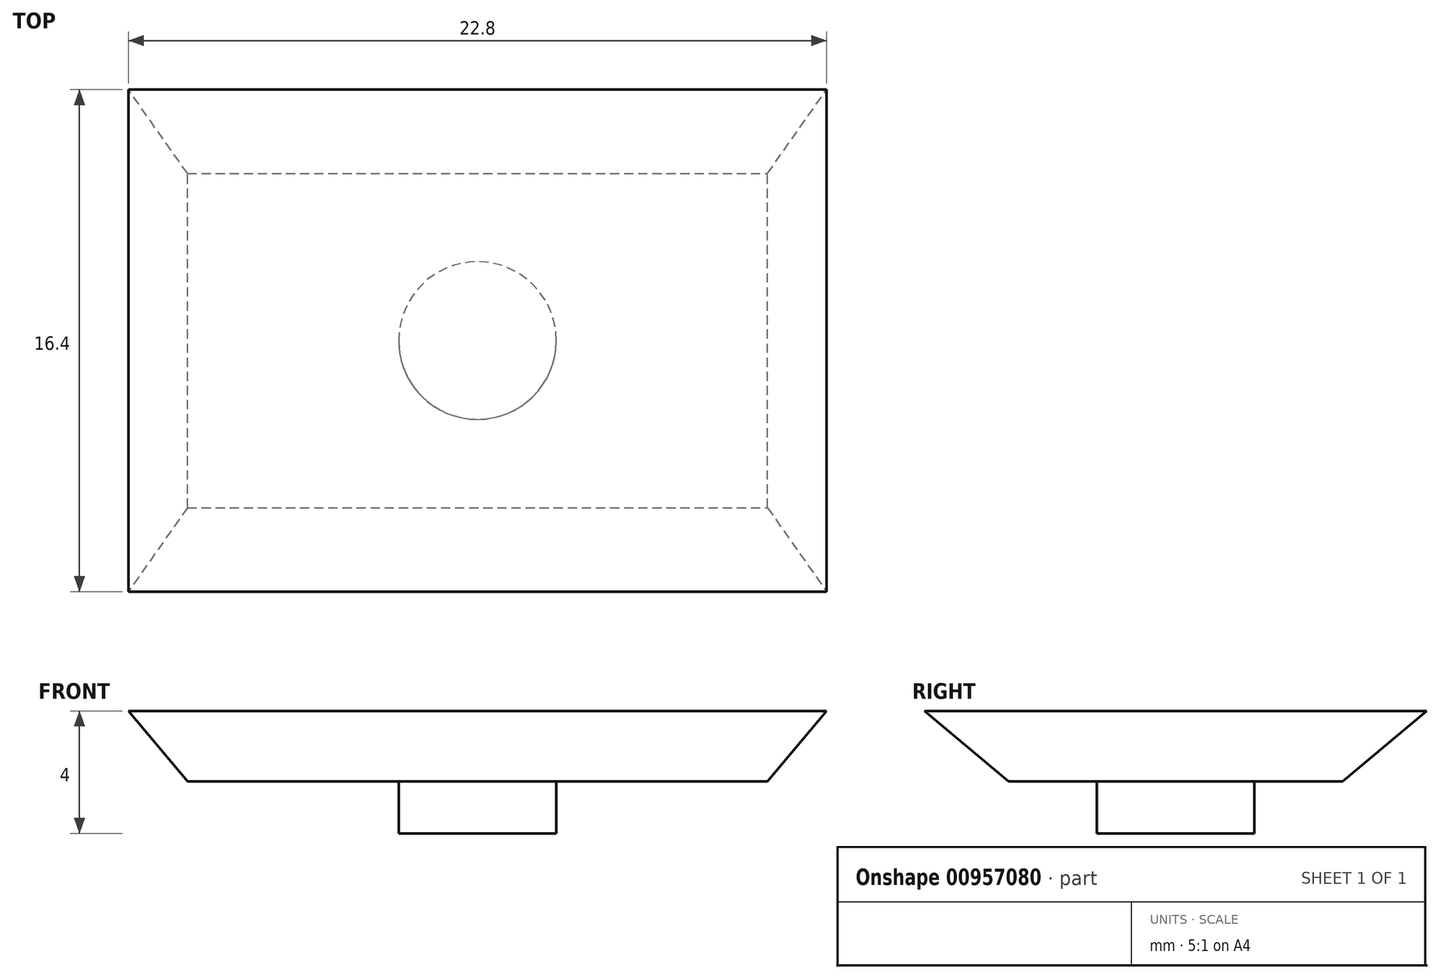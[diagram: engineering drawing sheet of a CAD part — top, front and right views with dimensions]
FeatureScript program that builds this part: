
annotation { "Feature Type Name" : "Feature", "Feature Type Description" : "" }
export const myFeature = defineFeature(function(context is Context, id is Id, definition is map)
    precondition{}
    {
        {
            var Q0;
            Q0=qCreatedBy(makeId("Front.planeOp"),FACE);
            var sketch = newSketch(context, id + "F0", { "sketchPlane" : qUnion([Q0])});
            skLineSegment(sketch, "E0", {"start": v(-15.47, 0) * mm, "end": v(15.77, 0) * mm, "construction": true});
            skLineSegment(sketch, "E1", {"start": v(0, 15.71) * mm, "end": v(0, -11.4) * mm, "construction": true});
            skLineSegment(sketch, "E2", {"start": v(0, 0) * mm, "end": v(9.47, 0) * mm});
            skLineSegment(sketch, "E3", {"start": v(9.47, 0) * mm, "end": v(11.4, 2.3) * mm});
            skLineSegment(sketch, "E4", {"start": v(11.4, 2.3) * mm, "end": v(0, 2.3) * mm});
            skLineSegment(sketch, "E5", {"start": v(9.47, 0) * mm, "end": v(9.47, 3.45) * mm, "construction": true});
            skLineSegment(sketch, "E6.MirrorCS", {"start": v(-11.4, 2.3) * mm, "end": v(0, 2.3) * mm});
            skLineSegment(sketch, "E7.MirrorCS", {"start": v(0, 0) * mm, "end": v(-9.47, 0) * mm});
            skLineSegment(sketch, "E8.MirrorCS", {"start": v(-9.47, 0) * mm, "end": v(-11.4, 2.3) * mm});
            skSolve(sketch);
        }
        {
            var Q0;
            Q0 = qSketchRegion(id + "F0", true);
            extrude(context, id + "F1", {"entities" : qUnion([Q0]), "depth" : 16.4 * mm, "offsetDistance" : 25 * mm});
        }
        {
            var Q0;
            Q0=qCreatedBy(makeId("Right.planeOp"),FACE);
            var sketch = newSketch(context, id + "F2", { "sketchPlane" : qUnion([Q0])});
            skLineSegment(sketch, "E9", {"start": v(0, 0) * mm, "end": v(-2.74, 0) * mm});
            skLineSegment(sketch, "E10", {"start": v(0, 2.3) * mm, "end": v(0, 0) * mm});
            skLineSegment(sketch, "E11", {"start": v(0, 2.3) * mm, "end": v(-2.74, 0) * mm});
            skLineSegment(sketch, "E12", {"start": v(-2.74, 0) * mm, "end": v(-2.74, 2.49) * mm, "construction": true});
            skLineSegment(sketch, "E13", {"start": v(-8.2, 6.19) * mm, "end": v(-8.2, -2.45) * mm, "construction": true});
            skLineSegment(sketch, "E14.MirrorCS", {"start": v(-16.4, 2.3) * mm, "end": v(-13.66, 0) * mm});
            skLineSegment(sketch, "E15.MirrorCS", {"start": v(-16.4, 0) * mm, "end": v(-13.66, 0) * mm});
            skLineSegment(sketch, "E16.MirrorCS", {"start": v(-16.4, 2.3) * mm, "end": v(-16.4, 0) * mm});
            skSolve(sketch);
        }
        {
            var Q0;
            Q0 = qSketchRegion(id + "F2", true);
            extrude(context, id + "F3", {"entities" : qUnion([Q0]), "operationType" : NewBodyOperationType.REMOVE, "endBound" : BoundingType.SYMMETRIC, "oppositeDirection" : true, "depth" : 25 * mm, "offsetDistance" : 25 * mm});
        }
        {
            var Q0;
            Q0=makeQuery(id+"F1.opExtrude","SWEPT_FACE",FACE,{"disambiguationData":[OSD([sQuery(id+"F0.wireOp",EDGE,"E4"),sQuery(id+"F0.wireOp",EDGE,"E6.MirrorCS")])]});
            var sketch = newSketch(context, id + "F4", { "sketchPlane" : qUnion([Q0])});
            skLineSegment(sketch, "E17", {"start": v(-11.4, 0) * mm, "end": v(13.98, 0) * mm, "construction": true});
            skLineSegment(sketch, "E18", {"start": v(0, 0) * mm, "end": v(0, -18.27) * mm, "construction": true});
            skLineSegment(sketch, "E19", {"start": v(-3.63, -8.2) * mm, "end": v(5.01, -8.2) * mm, "construction": true});
            skCircle(sketch, "E20", {"center": v(0, -8.2) * mm, "radius": 2.58 * mm});
            skSolve(sketch);
        }
        {
            var Q0;
            Q0 = qSketchRegion(id + "F4", true);
            extrude(context, id + "F5", {"entities" : qUnion([Q0]), "operationType" : NewBodyOperationType.ADD, "oppositeDirection" : true, "depth" : 4 * mm, "offsetDistance" : 25 * mm});
        }
    });
